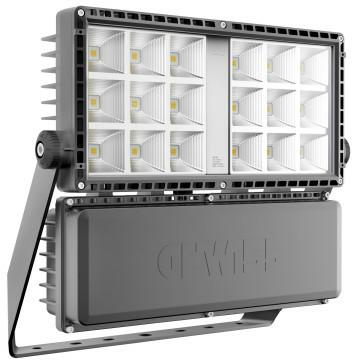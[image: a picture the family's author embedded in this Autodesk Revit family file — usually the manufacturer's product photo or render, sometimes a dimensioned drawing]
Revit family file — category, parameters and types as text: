
# Revit family: Lighting-Floodlights-GEWISS-SMART[PRO]2.0-LED-MEDIUM-POWER_2MODULE_CLI
name_source: partatom
category: Apparecchi per illuminazione
units: mm (PartAtom-declared; Revit-internal decimal feet)

## family parameters
Condiviso = No
Host = Superficie
Punto di calcolo locali = No
Quota connettore circolare = Usa diametro
Sorgente d'illuminazione = No
Taglio con vuoti quando caricato = No
Tipo di parte = Normale

## types (1)
- Lighting-Floodlights-GEWISS-SMART[PRO]2.0-LED-MEDIUM-POWER_2MODULE_CLI
    Applicazione = Indoor / Outdoor
    Body = Die-cast aluminium -
    Catalogue = LIGHTING
    Classification: = -
    Color Rendering Index = CRI-80
    Colour = Graphite grey
    Colour : = Polyester powder coated
    Colour temperature = 5700K
    Context = Sport, Big Areas
    Control System = Stand Alone - 1/10V
    DIN 18032-3 certification = Yes
    Descrizione = SMARTPRO2.0 2M 5700K CRI80 A3 1-10V CL1
    Device with reduced surface temperature = No
    Driver = Included
    Driver Box = Built-in
    Efficiency (lm/W) = 113
    Eletrical and lighting features = -
    External screw = Stainless steel
    Fixing = Bracket
    GW - Codice Electrocod = 2424
    Gasket = Anti-aging silicone
    General information = -
    Glow Wire Test : = -
    IDF = b469e256-7a48-4a8c-90a1-02dc77c86b94
    IDT = 94ca63f114e34adea3421514a6ca964f
    IP degree = IP66
    IPEA = ROAD = A // LARGE AREAS = A3 + // CYCLOPEDONALS = A + // GREEN AREAS = A + // HISTORICAL CENTER = A5 + // OTHER = A5 +
    Immagine tipo = GWP2275AS.jpg
    Installationa and maintenance = -
    Insulation class = I
    LED Maintenance = Not available
    Lampada = LED
    Lifetime = L90B10 (Tq+25°C) - 40000h L90B10 (Tq+50°C) = 32000h L80B10 (Tq+25°C) - 90000h
    Locking Hook = Hexagonal metric screws
    Lumen output (lm) = 37200
    Luminaire = LED luminaire with small,mid and high lumen power
    Materials = -
    Maximum surface exposed to the wind : = 0,170 m2
    Modello = GWP2285NS
    Mouting and installation = High-mast lighting - Wall mounting - Ground mouting
    Operating temperature : = -30 +50 °C
    Optic = A3 - Assymetric Narrow
    Optic : = Polished anodised aluminum reflector with 99.99% pure aluminum
    Optic Maintenance = Not available
    Optic and illuminating features = -
    Overvoltage protection = DM 5KV / CM 10KV
    Photobiological Risk Class = -
    Produttore = GEWISS S.p.A.
    Prospetto di default = 1219 mm
    Rated frequency (Hz) = 50 / 60
    SEO = Floodlight
    Shield type = Flat tempered glass 4mm
    Shock resistance = IK08
    Spostamento_x = 2186 mm
    Spostamento_x_effettivo = 1814 mm
    Standard Deviation Colour Matching = SDCM = 3
    Standard- = EN60598-1; EN60598-2-5; IEC 62778; IEC 62471; EN13201
    Standards and approvals = -
    Stocking temperature = -
    Supply voltage = 220 - 240 V
    System power = 330W
    Technical sheet = https://www.gewiss.com
    Tilt- = Rotation on bracket with integrated goniometer
    Type of light source = LED - Not replaceable
    URL = https://www.gewiss.com
    Unified Glare Rating = G*6 - ULOR = 0
    Unique digital code (Datamatrix) = Currently not present
    Version file RFA = 20.11
    Versions = 5700K cold light
    Warranty = 5 years
    Weight (kg): = 13
    Wiring = Watertight connector
